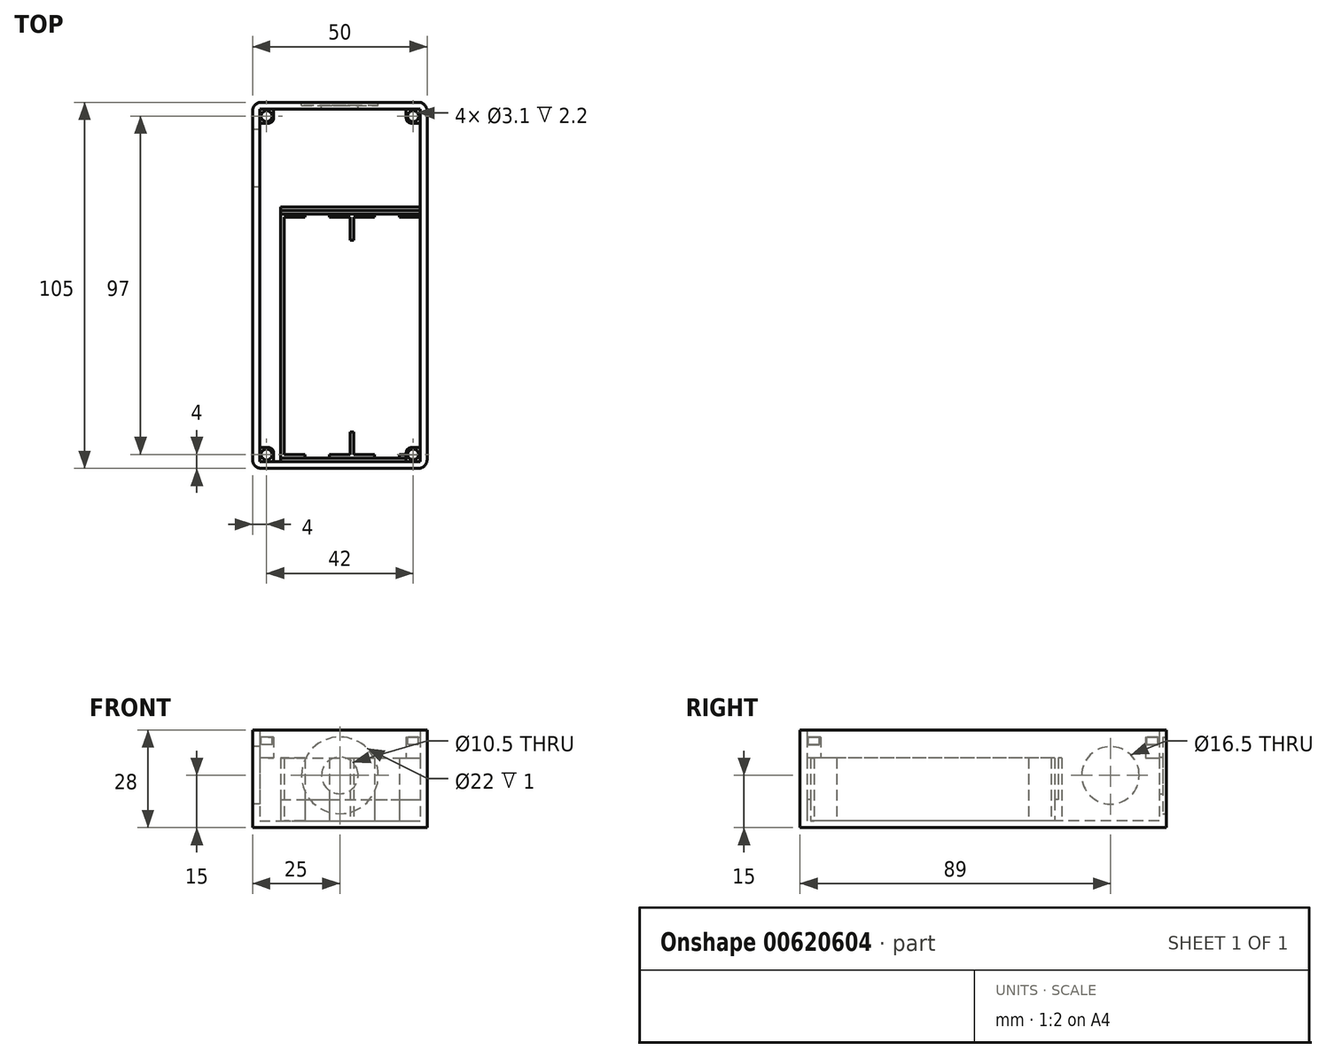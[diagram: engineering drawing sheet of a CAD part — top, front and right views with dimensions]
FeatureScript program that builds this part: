
annotation { "Feature Type Name" : "Feature", "Feature Type Description" : "" }
export const myFeature = defineFeature(function(context is Context, id is Id, definition is map)
    precondition{}
    {
        {
            assignVariable(context, id + "F0", {"name" : "Depth", "anyValue" : 30});
        }
        {
            assignVariable(context, id + "F1", {"name" : "WallThickness", "anyValue" : 2});
        }
        {
            assignVariable(context, id + "F2", {"name" : "Corner", "anyValue" : 2.5});
        }
        {
            var Q0;
            Q0=qCreatedBy(makeId("Top.planeOp"),FACE);
            var sketch = newSketch(context, id + "F3", { "sketchPlane" : qUnion([Q0])});
            skLineSegment(sketch, "E0.bottom", {"start": v(-25, 52.5) * mm, "end": v(25, 52.5) * mm});
            skLineSegment(sketch, "E0.top", {"start": v(-25, -52.5) * mm, "end": v(25, -52.5) * mm});
            skLineSegment(sketch, "E0.left", {"start": v(-25, 52.5) * mm, "end": v(-25, -52.5) * mm});
            skLineSegment(sketch, "E0.right", {"start": v(25, 52.5) * mm, "end": v(25, -52.5) * mm});
            skPoint(sketch, "E0.middle", {"position": v(0, 0) * mm});
            skSolve(sketch);
        }
        {
            var Q0;
            Q0 = qSketchRegion(id + "F3", true);
            extrude(context, id + "F4", {"entities" : qUnion([Q0]), "depth" : (getVariable(context, 'WallThickness')) * mm, "offsetDistance" : 25 * mm});
        }
        {
            var Q0;
            Q0=makeQuery(id+"F4.opExtrude","CAP_FACE",FACE,{"disambiguationData":[OSD([sQuery(id+"F3.wireOp",EDGE,"E0.bottom"),sQuery(id+"F3.wireOp",EDGE,"E0.top"),sQuery(id+"F3.wireOp",EDGE,"E0.left"),sQuery(id+"F3.wireOp",EDGE,"E0.right")])],"isStart":false});
            var sketch = newSketch(context, id + "F5", { "sketchPlane" : qUnion([Q0])});
            skLineSegment(sketch, "E1.bottom", {"start": v(-25, 52.5) * mm, "end": v(25, 52.5) * mm});
            skLineSegment(sketch, "E1.top", {"start": v(-25, -52.5) * mm, "end": v(25, -52.5) * mm});
            skLineSegment(sketch, "E1.left", {"start": v(-25, 52.5) * mm, "end": v(-25, -52.5) * mm});
            skLineSegment(sketch, "E1.right", {"start": v(25, 52.5) * mm, "end": v(25, -52.5) * mm});
            skPoint(sketch, "E1.middle", {"position": v(0, 0) * mm});
            skLineSegment(sketch, "E2.bottom", {"start": v(-23, 50.5) * mm, "end": v(23, 50.5) * mm});
            skLineSegment(sketch, "E2.top", {"start": v(-23, -50.5) * mm, "end": v(23, -50.5) * mm});
            skLineSegment(sketch, "E2.left", {"start": v(-23, 50.5) * mm, "end": v(-23, -50.5) * mm});
            skLineSegment(sketch, "E2.right", {"start": v(23, 50.5) * mm, "end": v(23, -50.5) * mm});
            skSolve(sketch);
        }
        {
            var Q0;
            Q0 = qSketchRegion(id + "F5", true);
            extrude(context, id + "F6", {"entities" : qUnion([Q0]), "operationType" : NewBodyOperationType.ADD, "depth" : (getVariable(context, 'Depth') - 2 * getVariable(context, 'WallThickness')) * mm, "offsetDistance" : 25 * mm});
        }
        {
            var Q0;
            Q0=makeQuery(id+"F6.boolean.opBoolean","MERGE",EDGE,{"derivedFrom":[makeQuery(id+"F4.opExtrude","SWEPT_EDGE",EDGE,{"disambiguationData":[OSD([sQuery(id+"F3.wireOp",EDGE,"E0.bottom"),sQuery(id+"F3.wireOp",EDGE,"E0.left")])]}),makeQuery(id+"F6.opExtrude","SWEPT_EDGE",EDGE,{"disambiguationData":[OSD([sQuery(id+"F5.wireOp",EDGE,"E1.bottom"),sQuery(id+"F5.wireOp",EDGE,"E1.left")])]})]});
            var Q1;
            Q1=makeQuery(id+"F6.boolean.opBoolean","MERGE",EDGE,{"derivedFrom":[makeQuery(id+"F4.opExtrude","SWEPT_EDGE",EDGE,{"disambiguationData":[OSD([sQuery(id+"F3.wireOp",EDGE,"E0.bottom"),sQuery(id+"F3.wireOp",EDGE,"E0.right")])]}),makeQuery(id+"F6.opExtrude","SWEPT_EDGE",EDGE,{"disambiguationData":[OSD([sQuery(id+"F5.wireOp",EDGE,"E1.bottom"),sQuery(id+"F5.wireOp",EDGE,"E1.right")])]})]});
            var Q2;
            Q2=makeQuery(id+"F6.boolean.opBoolean","MERGE",EDGE,{"derivedFrom":[makeQuery(id+"F4.opExtrude","SWEPT_EDGE",EDGE,{"disambiguationData":[OSD([sQuery(id+"F3.wireOp",EDGE,"E0.top"),sQuery(id+"F3.wireOp",EDGE,"E0.right")])]}),makeQuery(id+"F6.opExtrude","SWEPT_EDGE",EDGE,{"disambiguationData":[OSD([sQuery(id+"F5.wireOp",EDGE,"E1.top"),sQuery(id+"F5.wireOp",EDGE,"E1.right")])]})]});
            var Q3;
            Q3=makeQuery(id+"F6.boolean.opBoolean","MERGE",EDGE,{"derivedFrom":[makeQuery(id+"F4.opExtrude","SWEPT_EDGE",EDGE,{"disambiguationData":[OSD([sQuery(id+"F3.wireOp",EDGE,"E0.top"),sQuery(id+"F3.wireOp",EDGE,"E0.left")])]}),makeQuery(id+"F6.opExtrude","SWEPT_EDGE",EDGE,{"disambiguationData":[OSD([sQuery(id+"F5.wireOp",EDGE,"E1.top"),sQuery(id+"F5.wireOp",EDGE,"E1.left")])]})]});
            fillet(context, id + "F7", {"entities" : qUnion([Q0, Q1, Q2, Q3]), "radius" : (getVariable(context, 'Corner')) * mm, "tangentPropagation" : true, "allowEdgeOverflow" : false});
        }
        {
            var Q0;
            Q0=makeQuery(id+"F6.boolean.opBoolean","MERGE",FACE,{"derivedFrom":[makeQuery(id+"F4.opExtrude","SWEPT_FACE",FACE,{"disambiguationData":[OSD([sQuery(id+"F3.wireOp",EDGE,"E0.left")])]}),makeQuery(id+"F6.opExtrude","SWEPT_FACE",FACE,{"disambiguationData":[OSD([sQuery(id+"F5.wireOp",EDGE,"E1.left")])]})]});
            var sketch = newSketch(context, id + "F8", { "sketchPlane" : qUnion([Q0])});
            skCircle(sketch, "E3", {"center": v(-36.5, 15) * mm, "radius": 8.25 * mm});
            skSolve(sketch);
        }
        {
            var Q0;
            Q0 = qSketchRegion(id + "F8", true);
            extrude(context, id + "F9", {"entities" : qUnion([Q0]), "operationType" : NewBodyOperationType.REMOVE, "oppositeDirection" : true, "depth" : (getVariable(context, 'WallThickness')) * mm, "offsetDistance" : 25 * mm});
        }
        {
            var Q0;
            Q0=makeQuery(id+"F6.boolean.opBoolean","MERGE",FACE,{"derivedFrom":[makeQuery(id+"F4.opExtrude","SWEPT_FACE",FACE,{"disambiguationData":[OSD([sQuery(id+"F3.wireOp",EDGE,"E0.bottom")])]}),makeQuery(id+"F6.opExtrude","SWEPT_FACE",FACE,{"disambiguationData":[OSD([sQuery(id+"F5.wireOp",EDGE,"E1.bottom")])]})]});
            var sketch = newSketch(context, id + "F10", { "sketchPlane" : qUnion([Q0])});
            skCircle(sketch, "E4", {"center": v(0, 15) * mm, "radius": 5.25 * mm});
            skSolve(sketch);
        }
        {
            var Q0;
            Q0 = qSketchRegion(id + "F10", true);
            extrude(context, id + "F11", {"entities" : qUnion([Q0]), "operationType" : NewBodyOperationType.REMOVE, "oppositeDirection" : true, "depth" : (getVariable(context, 'WallThickness')) * mm, "offsetDistance" : 25 * mm});
        }
        {
            var Q0;
            Q0=makeQuery(id+"F6.boolean.opBoolean","MERGE",FACE,{"derivedFrom":[makeQuery(id+"F4.opExtrude","SWEPT_FACE",FACE,{"disambiguationData":[OSD([sQuery(id+"F3.wireOp",EDGE,"E0.bottom")])]}),makeQuery(id+"F6.opExtrude","SWEPT_FACE",FACE,{"disambiguationData":[OSD([sQuery(id+"F5.wireOp",EDGE,"E1.bottom")])]})]});
            var sketch = newSketch(context, id + "F12", { "sketchPlane" : qUnion([Q0])});
            skCircle(sketch, "E5", {"center": v(0, 15) * mm, "radius": 11 * mm});
            skSolve(sketch);
        }
        {
            var Q0;
            Q0=makeQuery(id+"F4.opExtrude","CAP_FACE",FACE,{"disambiguationData":[OSD([sQuery(id+"F3.wireOp",EDGE,"E0.bottom"),sQuery(id+"F3.wireOp",EDGE,"E0.top"),sQuery(id+"F3.wireOp",EDGE,"E0.left"),sQuery(id+"F3.wireOp",EDGE,"E0.right")])],"isStart":false});
            var sketch = newSketch(context, id + "F13", { "sketchPlane" : qUnion([Q0])});
            skLineSegment(sketch, "E6.bottom", {"start": v(17, 20.5) * mm, "end": v(23, 20.5) * mm});
            skLineSegment(sketch, "E6.top", {"start": v(17, 19.5) * mm, "end": v(23, 19.5) * mm});
            skLineSegment(sketch, "E6.left", {"start": v(17, 20.5) * mm, "end": v(17, 19.5) * mm});
            skLineSegment(sketch, "E6.right", {"start": v(23, 20.5) * mm, "end": v(23, 19.5) * mm});
            skLineSegment(sketch, "E7.bottom", {"start": v(17, -49.5) * mm, "end": v(23, -49.5) * mm});
            skLineSegment(sketch, "E7.top", {"start": v(17, -48.5) * mm, "end": v(23, -48.5) * mm});
            skLineSegment(sketch, "E7.left", {"start": v(17, -49.5) * mm, "end": v(17, -48.5) * mm});
            skLineSegment(sketch, "E7.right", {"start": v(23, -49.5) * mm, "end": v(23, -48.5) * mm});
            skLineSegment(sketch, "E8.bottom", {"start": v(-3, 20.5) * mm, "end": v(10, 20.5) * mm});
            skLineSegment(sketch, "E8.top", {"start": v(-3, 19.5) * mm, "end": v(10, 19.5) * mm});
            skLineSegment(sketch, "E8.left", {"start": v(-3, 20.5) * mm, "end": v(-3, 19.5) * mm});
            skLineSegment(sketch, "E8.right", {"start": v(10, 20.5) * mm, "end": v(10, 19.5) * mm});
            skLineSegment(sketch, "E9.bottom", {"start": v(-3, -49.5) * mm, "end": v(10, -49.5) * mm});
            skLineSegment(sketch, "E9.top", {"start": v(-3, -48.5) * mm, "end": v(10, -48.5) * mm});
            skLineSegment(sketch, "E9.left", {"start": v(-3, -49.5) * mm, "end": v(-3, -48.5) * mm});
            skLineSegment(sketch, "E9.right", {"start": v(10, -49.5) * mm, "end": v(10, -48.5) * mm});
            skLineSegment(sketch, "E10", {"start": v(3.5, 19.5) * mm, "end": v(3.5, -48.5) * mm, "construction": true});
            skLineSegment(sketch, "E11.bottom", {"start": v(3, 19.5) * mm, "end": v(4, 19.5) * mm});
            skLineSegment(sketch, "E11.top", {"start": v(3, -48.5) * mm, "end": v(4, -48.5) * mm});
            skLineSegment(sketch, "E11.left", {"start": v(3, 19.5) * mm, "end": v(3, 13) * mm});
            skLineSegment(sketch, "E11.right", {"start": v(4, 19.5) * mm, "end": v(4, 13) * mm});
            skPoint(sketch, "E11.middle", {"position": v(3.5, -14.5) * mm});
            skLineSegment(sketch, "E12", {"start": v(23, 19.5) * mm, "end": v(23, -48.5) * mm, "construction": true});
            skLineSegment(sketch, "E13.bottom", {"start": v(-10, 20.5) * mm, "end": v(-17, 20.5) * mm});
            skLineSegment(sketch, "E13.top", {"start": v(-10, 19.5) * mm, "end": v(-17, 19.5) * mm});
            skLineSegment(sketch, "E13.left", {"start": v(-10, 20.5) * mm, "end": v(-10, 19.5) * mm});
            skLineSegment(sketch, "E13.right", {"start": v(-17, 20.5) * mm, "end": v(-17, 19.5) * mm});
            skLineSegment(sketch, "E14.bottom", {"start": v(-17, -49.5) * mm, "end": v(-10, -49.5) * mm});
            skLineSegment(sketch, "E14.top", {"start": v(-17, -48.5) * mm, "end": v(-10, -48.5) * mm});
            skLineSegment(sketch, "E14.left", {"start": v(-17, -49.5) * mm, "end": v(-17, -48.5) * mm});
            skLineSegment(sketch, "E14.right", {"start": v(-10, -49.5) * mm, "end": v(-10, -48.5) * mm});
            skLineSegment(sketch, "E15.bottom", {"start": v(-17, 19.5) * mm, "end": v(-16, 19.5) * mm});
            skLineSegment(sketch, "E15.top", {"start": v(-17, -48.5) * mm, "end": v(-16, -48.5) * mm});
            skLineSegment(sketch, "E15.left", {"start": v(-17, 19.5) * mm, "end": v(-17, -48.5) * mm});
            skLineSegment(sketch, "E15.right", {"start": v(-16, 19.5) * mm, "end": v(-16, -48.5) * mm});
            skLineSegment(sketch, "E16.bottom", {"start": v(-17, 21.5) * mm, "end": v(23, 21.5) * mm});
            skLineSegment(sketch, "E16.top", {"start": v(-17, 22.5) * mm, "end": v(23, 22.5) * mm});
            skLineSegment(sketch, "E16.left", {"start": v(-17, 21.5) * mm, "end": v(-17, 22.5) * mm});
            skLineSegment(sketch, "E16.right", {"start": v(23, 21.5) * mm, "end": v(23, 22.5) * mm});
            skLineSegment(sketch, "E17", {"start": v(3, 13) * mm, "end": v(4, 13) * mm});
            skLineSegment(sketch, "E18", {"start": v(3, -42) * mm, "end": v(4, -42) * mm});
            skLineSegment(sketch, "E19.trimOffspring", {"start": v(3, -42) * mm, "end": v(3, -48.5) * mm});
            skLineSegment(sketch, "E20.trimOffspring", {"start": v(4, -42) * mm, "end": v(4, -48.5) * mm});
            skLineSegment(sketch, "E21", {"start": v(23, -49.5) * mm, "end": v(23, -50.5) * mm, "construction": true});
            skLineSegment(sketch, "E22", {"start": v(23, 20.5) * mm, "end": v(23, 21.5) * mm, "construction": true});
            skSolve(sketch);
        }
        {
            var Q0;
            Q0 = qSketchRegion(id + "F13", true);
            extrude(context, id + "F14", {"entities" : qUnion([Q0]), "operationType" : NewBodyOperationType.ADD, "depth" : 18 * mm, "offsetDistance" : 25 * mm});
        }
        {
            var Q0;
            Q0=makeQuery(id+"Fq0VFBIwur5QfF5_1.boolean.opBoolean","MERGE",FACE,{"derivedFrom":[makeQuery(id+"F4.opExtrude","CAP_FACE",FACE,{"disambiguationData":[OSD([sQuery(id+"F3.wireOp",EDGE,"E0.bottom"),sQuery(id+"F3.wireOp",EDGE,"E0.top"),sQuery(id+"F3.wireOp",EDGE,"E0.left"),sQuery(id+"F3.wireOp",EDGE,"E0.right")])],"isStart":false}),makeQuery(id+"Fq0VFBIwur5QfF5_1.opExtrude","CAP_FACE",FACE,{"disambiguationData":[OSD([sQuery(id+"Fw0MhdSW1QuX4eo_1.wireOp",EDGE,"shJbivPa-UgdR-oSKy-gT8v-vivpHOWCtKbI.bottom"),sQuery(id+"Fw0MhdSW1QuX4eo_1.wireOp",EDGE,"shJbivPa-UgdR-oSKy-gT8v-vivpHOWCtKbI.top"),sQuery(id+"Fw0MhdSW1QuX4eo_1.wireOp",EDGE,"shJbivPa-UgdR-oSKy-gT8v-vivpHOWCtKbI.left"),sQuery(id+"Fw0MhdSW1QuX4eo_1.wireOp",EDGE,"shJbivPa-UgdR-oSKy-gT8v-vivpHOWCtKbI.right")])],"isStart":true})]});
            var sketch = newSketch(context, id + "F15", { "sketchPlane" : qUnion([Q0])});
            skLineSegment(sketch, "E23.bottom", {"start": v(-17, 21.5) * mm, "end": v(23, 21.5) * mm});
            skLineSegment(sketch, "E23.top", {"start": v(-17, 20.5) * mm, "end": v(23, 20.5) * mm});
            skLineSegment(sketch, "E23.left", {"start": v(-17, 21.5) * mm, "end": v(-17, 20.5) * mm});
            skLineSegment(sketch, "E23.right", {"start": v(23, 21.5) * mm, "end": v(23, 20.5) * mm});
            skLineSegment(sketch, "E24.bottom", {"start": v(-17, -49.5) * mm, "end": v(23, -49.5) * mm});
            skLineSegment(sketch, "E24.top", {"start": v(-17, -50.5) * mm, "end": v(23, -50.5) * mm});
            skLineSegment(sketch, "E24.left", {"start": v(-17, -49.5) * mm, "end": v(-17, -50.5) * mm});
            skLineSegment(sketch, "E24.right", {"start": v(23, -49.5) * mm, "end": v(23, -50.5) * mm});
            skSolve(sketch);
        }
        {
            var Q0;
            Q0 = qSketchRegion(id + "F15", true);
            extrude(context, id + "F16", {"entities" : qUnion([Q0]), "operationType" : NewBodyOperationType.ADD, "depth" : 6 * mm, "offsetDistance" : 25 * mm});
        }
        {
            var Q0;
            Q0=makeQuery(id+"F14.opExtrude","CAP_FACE",FACE,{"disambiguationData":[OSD([sQuery(id+"F13.wireOp",EDGE,"E16.bottom"),sQuery(id+"F13.wireOp",EDGE,"E16.top"),sQuery(id+"F13.wireOp",EDGE,"E16.left"),sQuery(id+"F13.wireOp",EDGE,"E16.right")])],"isStart":false});
            var sketch = newSketch(context, id + "F17", { "sketchPlane" : qUnion([Q0])});
            skLineSegment(sketch, "E25.bottom", {"start": v(-20.5, 46.5) * mm, "end": v(-23, 46.5) * mm});
            skLineSegment(sketch, "E25.top", {"start": v(-19, 50.5) * mm, "end": v(-23, 50.5) * mm});
            skLineSegment(sketch, "E25.left", {"start": v(-19, 48) * mm, "end": v(-19, 50.5) * mm});
            skLineSegment(sketch, "E25.right", {"start": v(-23, 46.5) * mm, "end": v(-23, 50.5) * mm});
            skPoint(sketch, "E26.visualSharp", {"position": v(-19, 46.5) * mm});
            skArc(sketch, "E26.filletArc", {"start": v(-20.5, 46.5) * mm, "mid": v(-19.44, 46.94) * mm, "end": v(-19, 48) * mm});
            skArc(sketch, "E27.MirrorCS", {"start": v(20.5, 46.5) * mm, "mid": v(19.44, 46.94) * mm, "end": v(19, 48) * mm});
            skPoint(sketch, "E28.MirrorP", {"position": v(19, 46.5) * mm});
            skLineSegment(sketch, "E29.MirrorCS", {"start": v(20.5, 46.5) * mm, "end": v(23, 46.5) * mm});
            skLineSegment(sketch, "E30.MirrorCS", {"start": v(23, 46.5) * mm, "end": v(23, 50.5) * mm});
            skLineSegment(sketch, "E31.MirrorCS", {"start": v(19, 50.5) * mm, "end": v(23, 50.5) * mm});
            skLineSegment(sketch, "E32.MirrorCS", {"start": v(19, 48) * mm, "end": v(19, 50.5) * mm});
            skLineSegment(sketch, "E33.MirrorCS", {"start": v(19, -48) * mm, "end": v(19, -50.5) * mm});
            skLineSegment(sketch, "E34.MirrorCS", {"start": v(-20.5, -46.5) * mm, "end": v(-23, -46.5) * mm});
            skLineSegment(sketch, "E35.MirrorCS", {"start": v(-19, -48) * mm, "end": v(-19, -50.5) * mm});
            skLineSegment(sketch, "E36.MirrorCS", {"start": v(20.5, -46.5) * mm, "end": v(23, -46.5) * mm});
            skArc(sketch, "E37.MirrorCS", {"start": v(20.5, -46.5) * mm, "mid": v(19.44, -46.94) * mm, "end": v(19, -48) * mm});
            skArc(sketch, "E38.MirrorCS", {"start": v(-20.5, -46.5) * mm, "mid": v(-19.44, -46.94) * mm, "end": v(-19, -48) * mm});
            skLineSegment(sketch, "E39.MirrorCS", {"start": v(-19, -50.5) * mm, "end": v(-23, -50.5) * mm});
            skPoint(sketch, "E40.MirrorP", {"position": v(19, -46.5) * mm});
            skLineSegment(sketch, "E41.MirrorCS", {"start": v(23, -46.5) * mm, "end": v(23, -50.5) * mm});
            skLineSegment(sketch, "E42.MirrorCS", {"start": v(19, -50.5) * mm, "end": v(23, -50.5) * mm});
            skLineSegment(sketch, "E43.MirrorCS", {"start": v(-23, -46.5) * mm, "end": v(-23, -50.5) * mm});
            skPoint(sketch, "E44.MirrorP", {"position": v(-19, -46.5) * mm});
            skSolve(sketch);
        }
        {
            var Q0;
            Q0 = qSketchRegion(id + "F17", true);
            extrude(context, id + "F18", {"entities" : qUnion([Q0]), "operationType" : NewBodyOperationType.ADD, "depth" : 6 * mm, "offsetDistance" : 25 * mm});
        }
        {
            var Q0;
            Q0=makeQuery(id+"F18.opExtrude","CAP_FACE",FACE,{"disambiguationData":[OSD([sQuery(id+"F17.wireOp",EDGE,"E25.bottom"),sQuery(id+"F17.wireOp",EDGE,"E25.top"),sQuery(id+"F17.wireOp",EDGE,"E25.left"),sQuery(id+"F17.wireOp",EDGE,"E25.right"),sQuery(id+"F17.wireOp",EDGE,"E26.filletArc")])],"isStart":false});
            var sketch = newSketch(context, id + "F19", { "sketchPlane" : qUnion([Q0])});
            skCircle(sketch, "E45", {"center": v(-21, 48.5) * mm, "radius": 1.55 * mm});
            skPoint(sketch, "E45.centerSnap0", {"position": v(-23, 48.5) * mm});
            skPoint(sketch, "E45.centerSnap1", {"position": v(-21, 50.5) * mm});
            skPoint(sketch, "E46.MirrorP", {"position": v(21, 50.5) * mm});
            skCircle(sketch, "E47.MirrorC", {"center": v(21, 48.5) * mm, "radius": 1.55 * mm});
            skPoint(sketch, "E48.MirrorP", {"position": v(23, 48.5) * mm});
            skPoint(sketch, "E49.MirrorP", {"position": v(23, -48.5) * mm});
            skCircle(sketch, "E50.MirrorC", {"center": v(-21, -48.5) * mm, "radius": 1.55 * mm});
            skPoint(sketch, "E51.MirrorP", {"position": v(-21, -50.5) * mm});
            skCircle(sketch, "E52.MirrorC", {"center": v(21, -48.5) * mm, "radius": 1.55 * mm});
            skPoint(sketch, "E53.MirrorP", {"position": v(21, -50.5) * mm});
            skPoint(sketch, "E54.MirrorP", {"position": v(-23, -48.5) * mm});
            skSolve(sketch);
        }
        {
            var Q0;
            Q0 = qSketchRegion(id + "F19", true);
            extrude(context, id + "F20", {"entities" : qUnion([Q0]), "operationType" : NewBodyOperationType.REMOVE, "oppositeDirection" : true, "depth" : 2.2 * mm, "offsetDistance" : 25 * mm});
        }
        {
            var Q0;
            Q0 = qSketchRegion(id + "F12", true);
            extrude(context, id + "F21", {"entities" : qUnion([Q0]), "operationType" : NewBodyOperationType.REMOVE, "oppositeDirection" : true, "depth" : 1 * mm, "offsetDistance" : 25 * mm});
        }
    });
